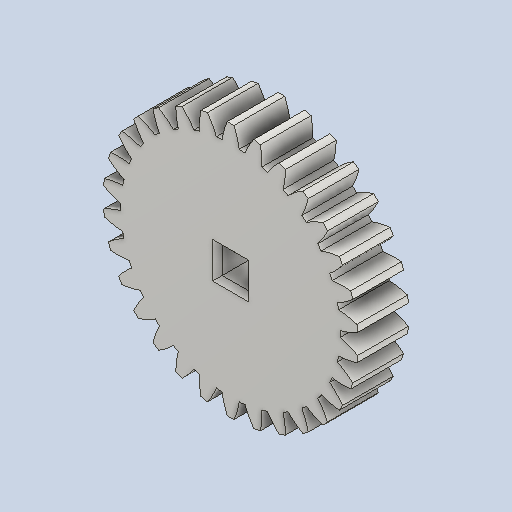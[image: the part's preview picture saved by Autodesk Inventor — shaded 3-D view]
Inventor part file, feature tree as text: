
AUTODESK INVENTOR PART (.ipt)
format: ipt  version: 2022 (Build 260153000, 153)  size: 619,520 bytes
history: native  units: mm (DEFAULTED — no unit token found)
features: plane x3, other x3, sketch x3, extrude x2, chamfer x1
ambient origin geometry x8: Origin, YZ Plane, XZ Plane, XY Plane, X Axis, Y Axis, Z Axis, Center Point
bodies: Solid1 (feature_tree)
feature tree (12):
  extrude  "Extrusion1"  Depth=6.35mm TaperAngle=0.0deg
  plane  "Work Plane1"
  plane  "Work Plane2"
  plane  "Work Plane3"
  other  "Spur Gear"
  extrude  "Extrusion2"  Depth=76.2mm TaperAngle=0.0deg
  chamfer  "Chamfer1"  Distance=1.047198mm
  sketch  "Sketch1"  dims[d0=31.912126mm d1=6.35mm d2=0.0mm]
  sketch  "Sketch2"  dims[d3=30.0mm d4=76.2mm d5=0.0mm d6=0.0mm d7=1.047198mm]
  other  "Srf1"
  sketch  "Sketch3"  dims[d9=0.0mm d14=0.0mm d15=25.4mm d16=0.0mm d17=0.0mm d18=0.0mm d19=25.4mm d20=3.325mm d21=0.0mm d22=0.0mm d23=0.6mm d24=3.175mm d25=45.0deg]
  other  "Pitch Diameter"
